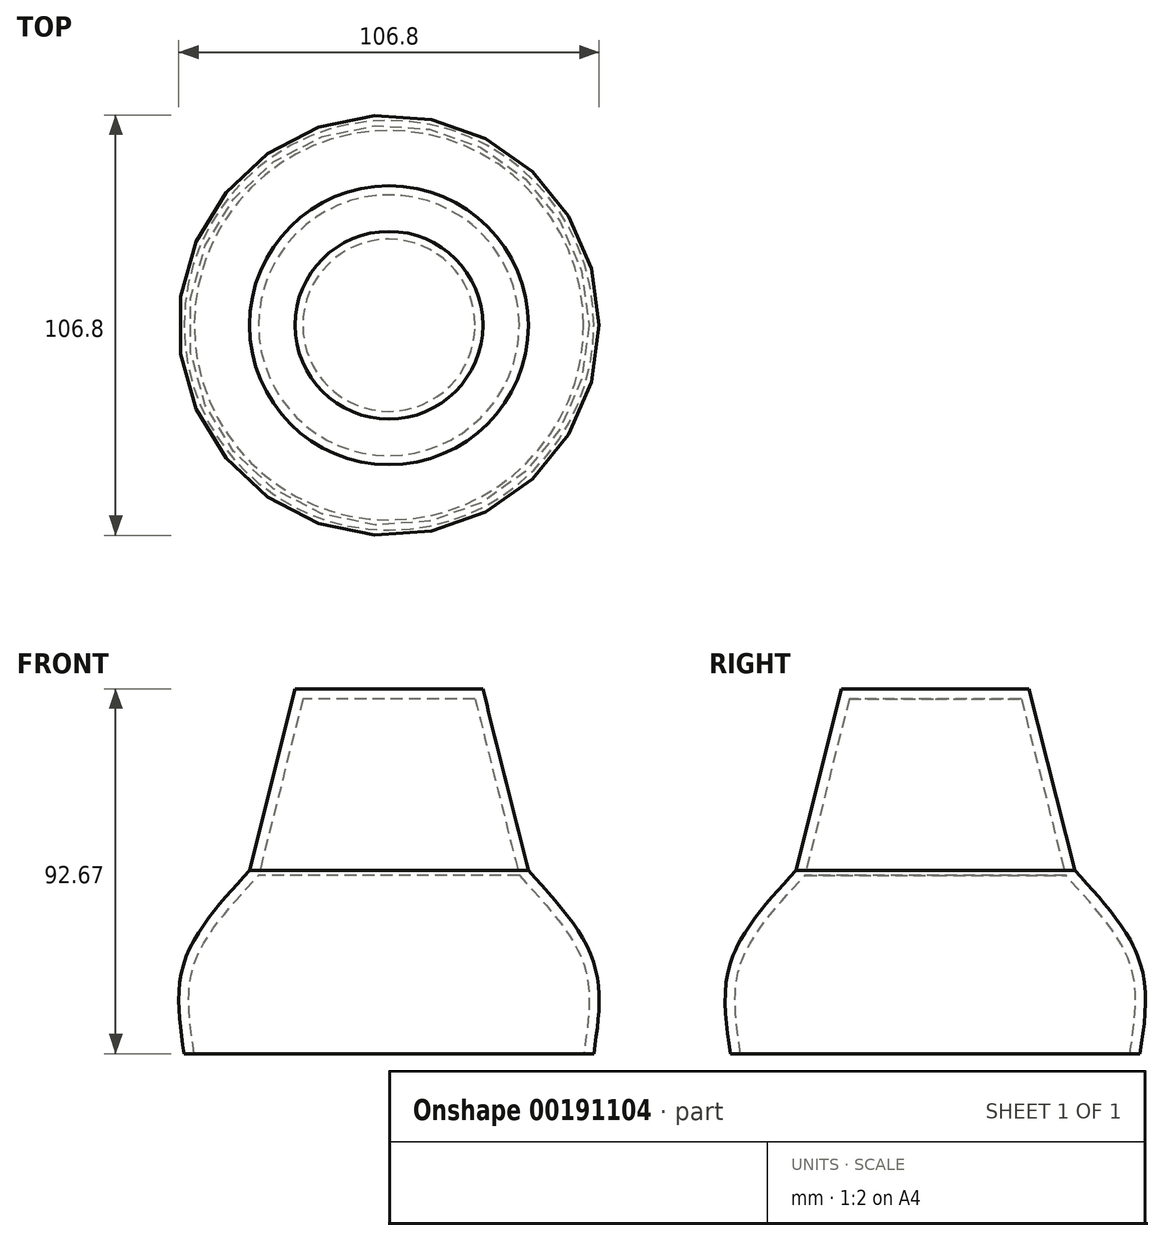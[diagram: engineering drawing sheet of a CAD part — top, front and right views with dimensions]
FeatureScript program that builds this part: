
annotation { "Feature Type Name" : "Feature", "Feature Type Description" : "" }
export const myFeature = defineFeature(function(context is Context, id is Id, definition is map)
    precondition{}
    {
        {
            var Q0;
            Q0=qCreatedBy(makeId("Front.planeOp"),FACE);
            var sketch = newSketch(context, id + "F0", { "sketchPlane" : qUnion([Q0])});
            skLineSegment(sketch, "E0", {"start": v(2.53, 27.83) * mm, "end": v(26.38, 27.83) * mm});
            skLineSegment(sketch, "E1", {"start": v(26.38, 27.83) * mm, "end": v(37.95, -18.32) * mm});
            skFitSpline(sketch, "E2", {"points": [v(37.95, -18.32) * mm, v(54.57, -41.7) * mm, v(54.57, -64.84) * mm], "startDerivative": vector(39.86, -43.2) * mm, "endDerivative": vector(-7.46, -49.96) * mm});
            skLineSegment(sketch, "E3", {"start": v(2.53, 27.83) * mm, "end": v(2.53, -64.84) * mm});
            skLineSegment(sketch, "E4", {"start": v(2.53, -64.84) * mm, "end": v(54.57, -64.84) * mm});
            skSolve(sketch);
        }
        {
            var Q0;
            Q0=makeQuery(id+"F0.imprint","IMPRINT",FACE,{"disambiguationData":[TD([[makeQuery(id+"F0.imprint","IMPRINT",EDGE,{"derivedFrom":sQuery(id+"F0.wireOp",EDGE,"E0")}),-1.0]])]});
            var Q1;
            Q1=sQuery(id+"F0.wireOp",EDGE,"E3");
            revolve(context, id + "F1", {"entities" : qUnion([Q0]), "axis" : qUnion([Q1]), "revolveType" : RevolveType.FULL});
        }
        {
            var Q0;
            Q0=makeQuery(id+"F1.opRevolve","SWEPT_FACE",FACE,{"disambiguationData":[OSD([sQuery(id+"F0.wireOp",EDGE,"E4")])]});
            shell(context, id + "F2", {"entities" : qUnion([Q0]), "thickness" : 2.54 * mm});
        }
    });
